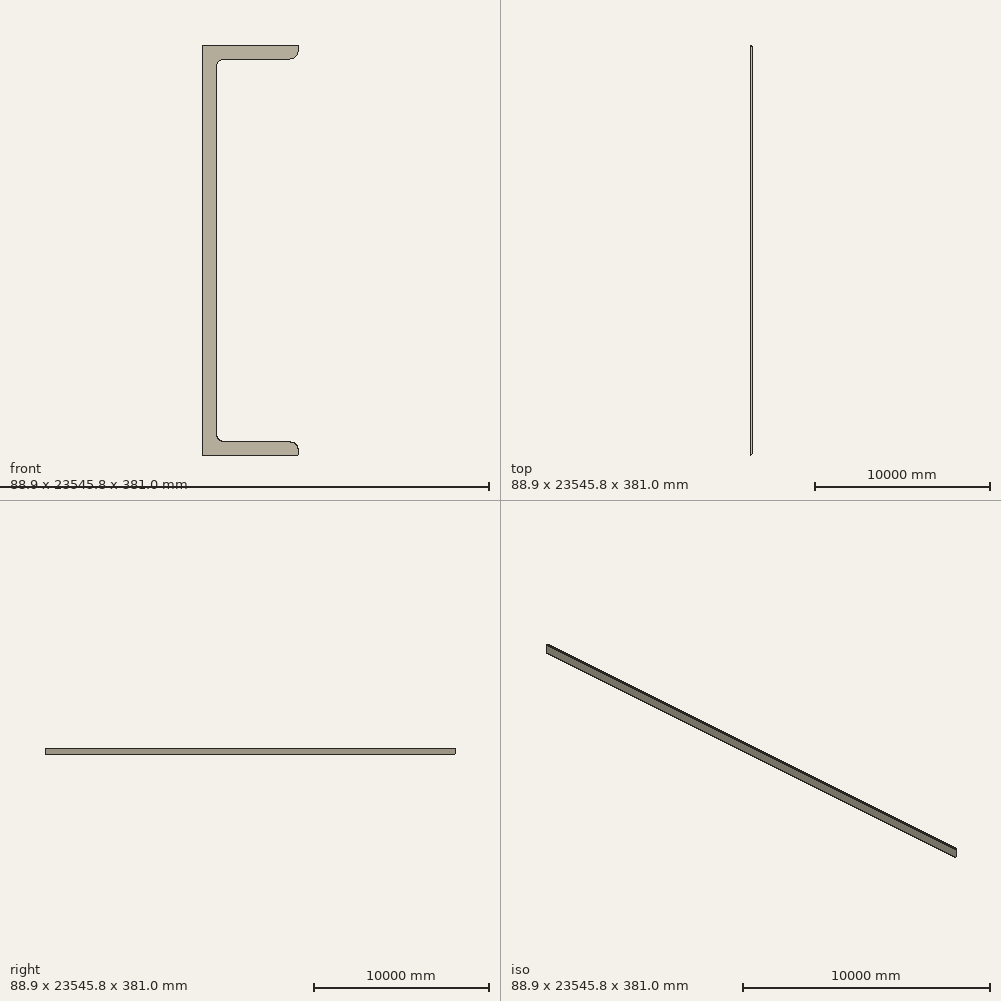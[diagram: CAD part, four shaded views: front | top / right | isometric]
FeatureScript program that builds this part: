
annotation { "Feature Type Name" : "Feature", "Feature Type Description" : "" }
export const myFeature = defineFeature(function(context is Context, id is Id, definition is map)
    precondition{}
    {
        {
            var Q0;
            Q0=qCreatedBy(makeId("Front.planeOp"),FACE);
            var sketch = newSketch(context, id + "F0", { "sketchPlane" : qUnion([Q0])});
            skLineSegment(sketch, "E0", {"start": v(44.45, 190.5) * mm, "end": v(-44.45, 190.5) * mm});
            skLineSegment(sketch, "E1", {"start": v(-44.45, 190.5) * mm, "end": v(-44.45, -190.5) * mm});
            skLineSegment(sketch, "E2", {"start": v(-44.45, -190.5) * mm, "end": v(44.45, -190.5) * mm});
            skLineSegment(sketch, "E3", {"start": v(44.45, -190.5) * mm, "end": v(44.45, -177.8) * mm});
            skLineSegment(sketch, "E4", {"start": v(44.45, -177.8) * mm, "end": v(-31.75, -177.8) * mm});
            skLineSegment(sketch, "E5", {"start": v(-31.75, -177.8) * mm, "end": v(-31.75, 177.8) * mm});
            skLineSegment(sketch, "E6", {"start": v(-31.75, 177.8) * mm, "end": v(44.45, 177.8) * mm});
            skLineSegment(sketch, "E7", {"start": v(44.45, 177.8) * mm, "end": v(44.45, 190.5) * mm});
            skSolve(sketch);
        }
        {
            var Q0;
            Q0=makeQuery(id+"F0.imprint","IMPRINT",FACE,{"disambiguationData":[TD([[makeQuery(id+"F0.imprint","IMPRINT",EDGE,{"derivedFrom":sQuery(id+"F0.wireOp",EDGE,"E0")}),1.0]])]});
            extrude(context, id + "F1", {"entities" : qUnion([Q0]), "depth" : 23469.6 * mm + 76.2 * mm, "offsetDistance" : 25.4 * mm});
        }
        {
            var Q0;
            Q0=makeQuery(id+"F1.opExtrude","SWEPT_EDGE",EDGE,{"disambiguationData":[OSD([sQuery(id+"F0.wireOp",EDGE,"E3"),sQuery(id+"F0.wireOp",EDGE,"E4")])]});
            var Q1;
            Q1=makeQuery(id+"F1.opExtrude","SWEPT_EDGE",EDGE,{"disambiguationData":[OSD([sQuery(id+"F0.wireOp",EDGE,"E4"),sQuery(id+"F0.wireOp",EDGE,"E5")])]});
            var Q2;
            Q2=makeQuery(id+"F1.opExtrude","SWEPT_EDGE",EDGE,{"disambiguationData":[OSD([sQuery(id+"F0.wireOp",EDGE,"E5"),sQuery(id+"F0.wireOp",EDGE,"E6")])]});
            var Q3;
            Q3=makeQuery(id+"F1.opExtrude","SWEPT_EDGE",EDGE,{"disambiguationData":[OSD([sQuery(id+"F0.wireOp",EDGE,"E6"),sQuery(id+"F0.wireOp",EDGE,"E7")])]});
            fillet(context, id + "F2", {"entities" : qUnion([Q0, Q1, Q2, Q3]), "radius" : 7.62 * mm, "tangentPropagation" : true, "allowEdgeOverflow" : false});
        }
        {
            var Q0;
            Q0=makeQuery(id+"F1.opExtrude","SWEPT_FACE",FACE,{"disambiguationData":[OSD([sQuery(id+"F0.wireOp",EDGE,"E0")])]});
            var sketch = newSketch(context, id + "F3", { "sketchPlane" : qUnion([Q0])});
            skLineSegment(sketch, "E8", {"start": v(-44.45, 0) * mm, "end": v(44.45, -88.9) * mm});
            skLineSegment(sketch, "E9", {"start": v(-44.45, -23545.8) * mm, "end": v(44.45, -23456.9) * mm});
            skSolve(sketch);
        }
        {
            var Q0;
            {var subQ0=sQuery(id+"F3.wireOp",EDGE,"E8");Q0=makeQuery(id+"F3.imprint","IMPRINT",FACE,{"disambiguationData":[TD([[makeQuery(id+"F3.imprint","IMPRINT",EDGE,{"derivedFrom":subQ0}),1.0]])]});}
            extrude(context, id + "F4", {"entities" : qUnion([Q0]), "operationType" : NewBodyOperationType.REMOVE, "endBound" : BoundingType.THROUGH_ALL, "oppositeDirection" : true, "depth" : 25.4 * mm});
        }
        {
            var Q0;
            {var subQ0=sQuery(id+"F3.wireOp",EDGE,"E9");Q0=makeQuery(id+"F3.imprint","IMPRINT",FACE,{"disambiguationData":[TD([[makeQuery(id+"F3.imprint","IMPRINT",EDGE,{"derivedFrom":subQ0}),-1.0]])]});}
            extrude(context, id + "F5", {"entities" : qUnion([Q0]), "operationType" : NewBodyOperationType.REMOVE, "endBound" : BoundingType.THROUGH_ALL, "oppositeDirection" : true, "depth" : 25.4 * mm});
        }
    });
